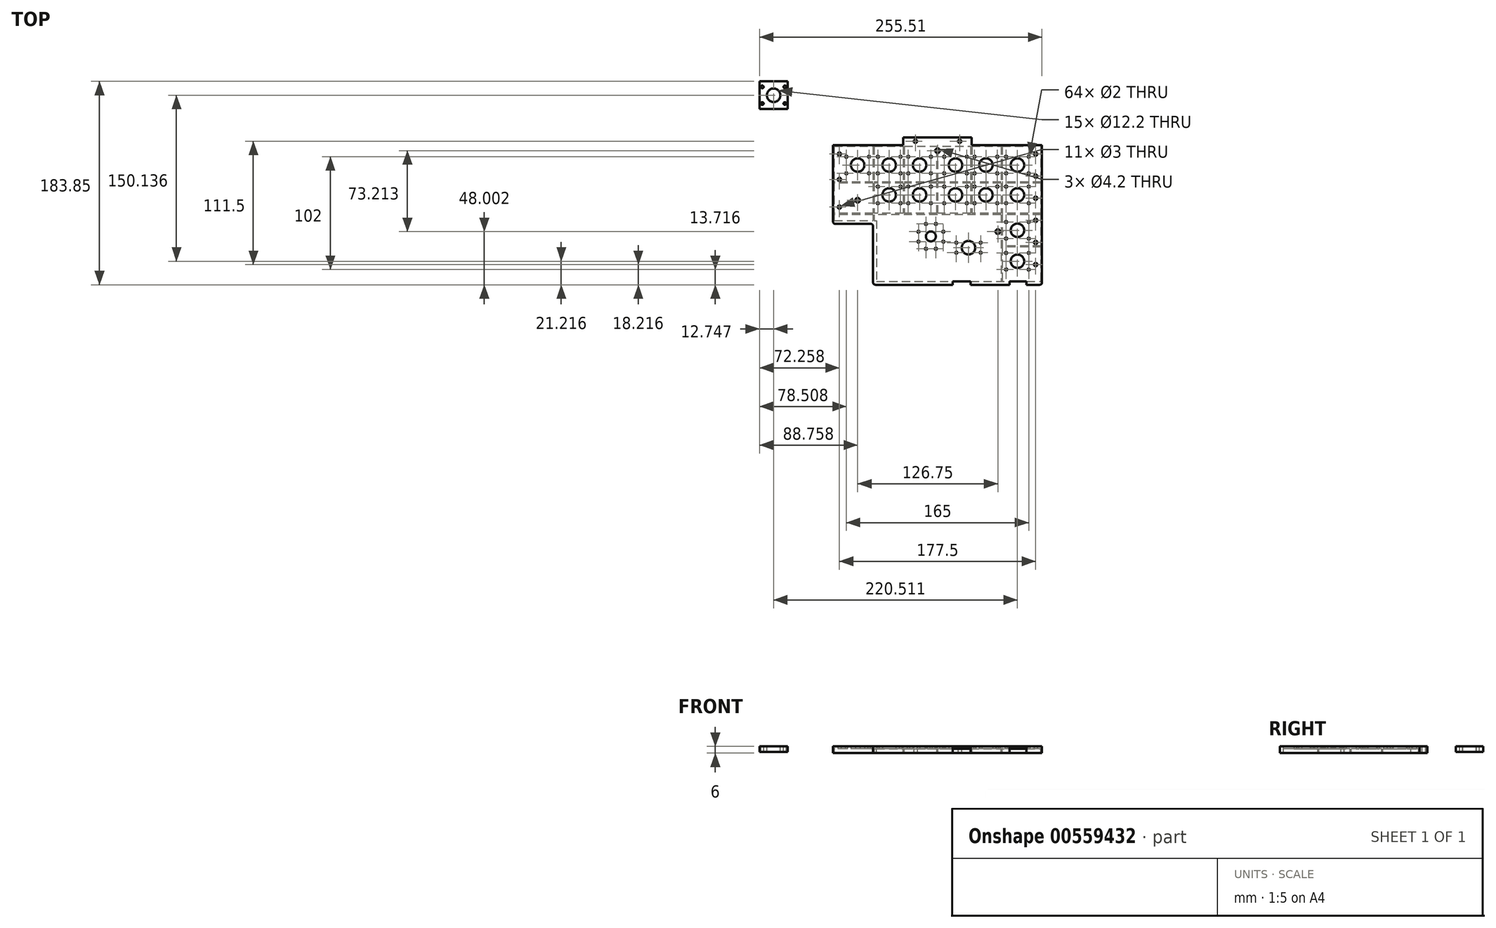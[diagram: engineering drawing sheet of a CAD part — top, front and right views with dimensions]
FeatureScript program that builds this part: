
annotation { "Feature Type Name" : "Feature", "Feature Type Description" : "" }
export const myFeature = defineFeature(function(context is Context, id is Id, definition is map)
    precondition{}
    {
        {
            var Q0;
            Q0=qCreatedBy(makeId("Top.planeOp"),FACE);
            var sketch = newSketch(context, id + "F0", { "sketchPlane" : qUnion([Q0])});
            skLineSegment(sketch, "E0.bottom", {"start": v(3.56, -143.75) * mm, "end": v(29.06, -143.75) * mm, "construction": true});
            skLineSegment(sketch, "E0.top", {"start": v(3.56, -173.75) * mm, "end": v(29.06, -173.75) * mm, "construction": true});
            skLineSegment(sketch, "E0.left", {"start": v(3.56, -143.75) * mm, "end": v(3.56, -173.75) * mm, "construction": true});
            skLineSegment(sketch, "E0.right", {"start": v(29.06, -143.75) * mm, "end": v(29.06, -173.75) * mm, "construction": true});
            skLineSegment(sketch, "E1.bottom", {"start": v(32.06, -143.75) * mm, "end": v(57.56, -143.75) * mm, "construction": true});
            skLineSegment(sketch, "E1.top", {"start": v(32.06, -173.75) * mm, "end": v(57.56, -173.75) * mm, "construction": true});
            skLineSegment(sketch, "E1.left", {"start": v(32.06, -143.75) * mm, "end": v(32.06, -173.75) * mm, "construction": true});
            skLineSegment(sketch, "E1.right", {"start": v(57.56, -143.75) * mm, "end": v(57.56, -173.75) * mm, "construction": true});
            skLineSegment(sketch, "E2.bottom", {"start": v(119.56, -143.75) * mm, "end": v(145.06, -143.75) * mm, "construction": true});
            skLineSegment(sketch, "E2.top", {"start": v(119.56, -173.75) * mm, "end": v(145.06, -173.75) * mm, "construction": true});
            skLineSegment(sketch, "E2.left", {"start": v(119.56, -143.75) * mm, "end": v(119.56, -173.75) * mm, "construction": true});
            skLineSegment(sketch, "E2.right", {"start": v(145.06, -143.75) * mm, "end": v(145.06, -173.75) * mm, "construction": true});
            skLineSegment(sketch, "E3.bottom", {"start": v(148.06, -143.75) * mm, "end": v(173.56, -143.75) * mm, "construction": true});
            skLineSegment(sketch, "E3.top", {"start": v(148.06, -173.75) * mm, "end": v(173.56, -173.75) * mm, "construction": true});
            skLineSegment(sketch, "E3.left", {"start": v(148.06, -143.75) * mm, "end": v(148.06, -173.75) * mm, "construction": true});
            skLineSegment(sketch, "E3.right", {"start": v(173.56, -143.75) * mm, "end": v(173.56, -173.75) * mm, "construction": true});
            skLineSegment(sketch, "E4.top", {"start": v(148.06, -206.75) * mm, "end": v(173.56, -206.75) * mm, "construction": true});
            skLineSegment(sketch, "E5.bottom", {"start": v(148.06, -209.25) * mm, "end": v(173.56, -209.25) * mm, "construction": true});
            skLineSegment(sketch, "E5.top", {"start": v(148.06, -239.25) * mm, "end": v(173.56, -239.25) * mm, "construction": true});
            skLineSegment(sketch, "E5.left", {"start": v(148.06, -209.25) * mm, "end": v(148.06, -239.25) * mm, "construction": true});
            skLineSegment(sketch, "E5.right", {"start": v(173.56, -209.25) * mm, "end": v(173.56, -239.25) * mm, "construction": true});
            skLineSegment(sketch, "E6.bottom", {"start": v(-4.94, -140.75) * mm, "end": v(182.06, -140.75) * mm});
            skLineSegment(sketch, "E6.top", {"start": v(33.28, -263.97) * mm, "end": v(182.06, -263.97) * mm});
            skLineSegment(sketch, "E6.left", {"start": v(-4.94, -140.75) * mm, "end": v(-4.94, -208.97) * mm});
            skLineSegment(sketch, "E6.right", {"start": v(182.06, -140.75) * mm, "end": v(182.06, -263.97) * mm});
            skLineSegment(sketch, "E7", {"start": v(-4.94, -208.97) * mm, "end": v(33.28, -208.97) * mm});
            skLineSegment(sketch, "E8", {"start": v(33.28, -208.97) * mm, "end": v(33.28, -263.97) * mm});
            skLineSegment(sketch, "E9.bottom", {"start": v(-67.45, -83.12) * mm, "end": v(-51.95, -83.12) * mm});
            skLineSegment(sketch, "E9.top", {"start": v(-67.45, -108.12) * mm, "end": v(-51.95, -108.12) * mm});
            skLineSegment(sketch, "E9.left", {"start": v(-67.45, -83.12) * mm, "end": v(-67.45, -108.12) * mm});
            skLineSegment(sketch, "E9.right", {"start": v(-51.95, -83.12) * mm, "end": v(-51.95, -108.12) * mm});
            skLineSegment(sketch, "E10.bottom", {"start": v(-51.95, -83.12) * mm, "end": v(-46.95, -83.12) * mm});
            skLineSegment(sketch, "E10.top", {"start": v(-51.95, -108.12) * mm, "end": v(-46.95, -108.12) * mm});
            skLineSegment(sketch, "E10.right", {"start": v(-46.95, -83.12) * mm, "end": v(-46.95, -108.12) * mm});
            skLineSegment(sketch, "E11.bottom", {"start": v(-67.45, -83.12) * mm, "end": v(-72.45, -83.12) * mm});
            skLineSegment(sketch, "E11.top", {"start": v(-67.45, -108.12) * mm, "end": v(-72.45, -108.12) * mm});
            skLineSegment(sketch, "E11.right", {"start": v(-72.45, -83.12) * mm, "end": v(-72.45, -108.12) * mm});
            skCircle(sketch, "E12", {"center": v(-59.7, -95.62) * mm, "radius": 6.1 * mm});
            skPoint(sketch, "E12.centerSnap0", {"position": v(-67.45, -95.62) * mm});
            skPoint(sketch, "E12.centerSnap1", {"position": v(-59.7, -83.12) * mm});
            skCircle(sketch, "E13", {"center": v(-69.95, -88.12) * mm, "radius": 1.25 * mm});
            skPoint(sketch, "E13.centerSnap0", {"position": v(-69.95, -83.12) * mm});
            skCircle(sketch, "E14", {"center": v(-69.95, -103.12) * mm, "radius": 1.25 * mm});
            skCircle(sketch, "E15", {"center": v(-49.45, -88.12) * mm, "radius": 1.25 * mm});
            skPoint(sketch, "E15.centerSnap0", {"position": v(-49.45, -83.12) * mm});
            skCircle(sketch, "E16", {"center": v(-49.45, -103.12) * mm, "radius": 1.25 * mm});
            skLineSegment(sketch, "E17.bottom", {"start": v(3.56, -146.25) * mm, "end": v(8.56, -146.25) * mm, "construction": true});
            skLineSegment(sketch, "E17.top", {"start": v(3.56, -171.25) * mm, "end": v(8.56, -171.25) * mm, "construction": true});
            skLineSegment(sketch, "E17.left", {"start": v(3.56, -146.25) * mm, "end": v(3.56, -171.25) * mm, "construction": true});
            skLineSegment(sketch, "E17.right", {"start": v(8.56, -146.25) * mm, "end": v(8.56, -171.25) * mm, "construction": true});
            skLineSegment(sketch, "E18.bottom", {"start": v(29.06, -146.25) * mm, "end": v(24.06, -146.25) * mm, "construction": true});
            skLineSegment(sketch, "E18.top", {"start": v(29.06, -171.25) * mm, "end": v(24.06, -171.25) * mm, "construction": true});
            skLineSegment(sketch, "E18.left", {"start": v(29.06, -146.25) * mm, "end": v(29.06, -171.25) * mm, "construction": true});
            skLineSegment(sketch, "E18.right", {"start": v(24.06, -146.25) * mm, "end": v(24.06, -171.25) * mm, "construction": true});
            skCircle(sketch, "E19", {"center": v(6.06, -151.25) * mm, "radius": 1 * mm});
            skPoint(sketch, "E19.centerSnap0", {"position": v(6.06, -146.25) * mm});
            skCircle(sketch, "E20", {"center": v(6.06, -166.25) * mm, "radius": 1 * mm});
            skCircle(sketch, "E21", {"center": v(16.3, -158.75) * mm, "radius": 6.1 * mm});
            skPoint(sketch, "E21.centerSnap0", {"position": v(8.56, -158.75) * mm});
            skPoint(sketch, "E21.centerSnap1", {"position": v(16.3, -143.75) * mm});
            skCircle(sketch, "E22", {"center": v(26.56, -151.25) * mm, "radius": 1 * mm});
            skPoint(sketch, "E22.centerSnap0", {"position": v(26.56, -146.25) * mm});
            skCircle(sketch, "E23", {"center": v(26.56, -166.25) * mm, "radius": 1 * mm});
            skCircle(sketch, "E24", {"center": v(105.56, -228.97) * mm, "radius": 1 * mm});
            skCircle(sketch, "E25", {"center": v(105.56, -237.97) * mm, "radius": 1 * mm});
            skCircle(sketch, "E26", {"center": v(127.56, -228.97) * mm, "radius": 1 * mm});
            skCircle(sketch, "E27", {"center": v(127.56, -237.97) * mm, "radius": 1 * mm});
            skLineSegment(sketch, "E28.bottom", {"start": v(151.56, -240.25) * mm, "end": v(173.56, -240.25) * mm, "construction": true});
            skLineSegment(sketch, "E28.top", {"start": v(151.56, -262.25) * mm, "end": v(173.56, -262.25) * mm, "construction": true});
            skLineSegment(sketch, "E28.left", {"start": v(151.56, -240.25) * mm, "end": v(151.56, -262.25) * mm, "construction": true});
            skLineSegment(sketch, "E28.right", {"start": v(173.56, -240.25) * mm, "end": v(173.56, -262.25) * mm, "construction": true});
            skLineSegment(sketch, "E29.bottom", {"start": v(154.8, -239.75) * mm, "end": v(166.8, -239.75) * mm, "construction": true});
            skLineSegment(sketch, "E29.top", {"start": v(154.8, -251.75) * mm, "end": v(166.8, -251.75) * mm, "construction": true});
            skLineSegment(sketch, "E29.left", {"start": v(154.8, -239.75) * mm, "end": v(154.8, -251.75) * mm, "construction": true});
            skLineSegment(sketch, "E29.right", {"start": v(166.8, -239.75) * mm, "end": v(166.8, -251.75) * mm, "construction": true});
            skLineSegment(sketch, "E30.bottom", {"start": v(32.06, -146.25) * mm, "end": v(37.06, -146.25) * mm, "construction": true});
            skLineSegment(sketch, "E30.top", {"start": v(32.06, -171.25) * mm, "end": v(37.06, -171.25) * mm, "construction": true});
            skLineSegment(sketch, "E30.left", {"start": v(32.06, -146.25) * mm, "end": v(32.06, -171.25) * mm, "construction": true});
            skLineSegment(sketch, "E30.right", {"start": v(37.06, -146.25) * mm, "end": v(37.06, -171.25) * mm, "construction": true});
            skLineSegment(sketch, "E31.bottom", {"start": v(57.56, -146.25) * mm, "end": v(52.56, -146.25) * mm, "construction": true});
            skLineSegment(sketch, "E31.top", {"start": v(57.56, -171.25) * mm, "end": v(52.56, -171.25) * mm, "construction": true});
            skLineSegment(sketch, "E31.left", {"start": v(57.56, -146.25) * mm, "end": v(57.56, -171.25) * mm, "construction": true});
            skLineSegment(sketch, "E31.right", {"start": v(52.56, -146.25) * mm, "end": v(52.56, -171.25) * mm, "construction": true});
            skCircle(sketch, "E32", {"center": v(34.56, -151.25) * mm, "radius": 1 * mm});
            skPoint(sketch, "E32.centerSnap0", {"position": v(34.56, -146.25) * mm});
            skCircle(sketch, "E33", {"center": v(34.56, -166.25) * mm, "radius": 1 * mm});
            skCircle(sketch, "E34", {"center": v(55.06, -151.25) * mm, "radius": 1 * mm});
            skPoint(sketch, "E34.centerSnap0", {"position": v(55.06, -146.25) * mm});
            skCircle(sketch, "E35", {"center": v(55.06, -166.25) * mm, "radius": 1 * mm});
            skCircle(sketch, "E36", {"center": v(44.8, -158.75) * mm, "radius": 6.1 * mm});
            skPoint(sketch, "E36.centerSnap0", {"position": v(37.06, -158.75) * mm});
            skPoint(sketch, "E36.centerSnap1", {"position": v(44.8, -143.75) * mm});
            skLineSegment(sketch, "E37.bottom", {"start": v(119.56, -146.25) * mm, "end": v(124.56, -146.25) * mm, "construction": true});
            skLineSegment(sketch, "E37.top", {"start": v(119.56, -171.25) * mm, "end": v(124.56, -171.25) * mm, "construction": true});
            skLineSegment(sketch, "E37.left", {"start": v(119.56, -146.25) * mm, "end": v(119.56, -171.25) * mm, "construction": true});
            skLineSegment(sketch, "E37.right", {"start": v(124.56, -146.25) * mm, "end": v(124.56, -171.25) * mm, "construction": true});
            skLineSegment(sketch, "E38.bottom", {"start": v(145.06, -146.25) * mm, "end": v(140.06, -146.25) * mm, "construction": true});
            skLineSegment(sketch, "E38.top", {"start": v(145.06, -171.25) * mm, "end": v(140.06, -171.25) * mm, "construction": true});
            skLineSegment(sketch, "E38.left", {"start": v(145.06, -146.25) * mm, "end": v(145.06, -171.25) * mm, "construction": true});
            skLineSegment(sketch, "E38.right", {"start": v(140.06, -146.25) * mm, "end": v(140.06, -171.25) * mm, "construction": true});
            skLineSegment(sketch, "E39.bottom", {"start": v(148.06, -146.25) * mm, "end": v(153.06, -146.25) * mm, "construction": true});
            skLineSegment(sketch, "E39.top", {"start": v(148.06, -171.25) * mm, "end": v(153.06, -171.25) * mm, "construction": true});
            skLineSegment(sketch, "E39.left", {"start": v(148.06, -146.25) * mm, "end": v(148.06, -171.25) * mm, "construction": true});
            skLineSegment(sketch, "E39.right", {"start": v(153.06, -146.25) * mm, "end": v(153.06, -171.25) * mm, "construction": true});
            skLineSegment(sketch, "E40.bottom", {"start": v(173.56, -146.25) * mm, "end": v(168.56, -146.25) * mm, "construction": true});
            skLineSegment(sketch, "E40.top", {"start": v(173.56, -171.25) * mm, "end": v(168.56, -171.25) * mm, "construction": true});
            skLineSegment(sketch, "E40.left", {"start": v(173.56, -146.25) * mm, "end": v(173.56, -171.25) * mm, "construction": true});
            skLineSegment(sketch, "E40.right", {"start": v(168.56, -146.25) * mm, "end": v(168.56, -171.25) * mm, "construction": true});
            skLineSegment(sketch, "E41.top", {"start": v(148.06, -204.25) * mm, "end": v(153.06, -204.25) * mm, "construction": true});
            skLineSegment(sketch, "E42.top", {"start": v(173.56, -204.25) * mm, "end": v(168.56, -204.25) * mm, "construction": true});
            skLineSegment(sketch, "E43.bottom", {"start": v(148.06, -205.25) * mm, "end": v(153.06, -205.25) * mm, "construction": true});
            skLineSegment(sketch, "E43.top", {"start": v(148.06, -230.25) * mm, "end": v(153.06, -230.25) * mm, "construction": true});
            skLineSegment(sketch, "E43.left", {"start": v(148.06, -205.25) * mm, "end": v(148.06, -230.25) * mm, "construction": true});
            skLineSegment(sketch, "E43.right", {"start": v(153.06, -205.25) * mm, "end": v(153.06, -230.25) * mm, "construction": true});
            skLineSegment(sketch, "E44.bottom", {"start": v(173.56, -205.25) * mm, "end": v(168.56, -205.25) * mm, "construction": true});
            skLineSegment(sketch, "E44.top", {"start": v(173.56, -230.25) * mm, "end": v(168.56, -230.25) * mm, "construction": true});
            skLineSegment(sketch, "E44.left", {"start": v(173.56, -205.25) * mm, "end": v(173.56, -230.25) * mm, "construction": true});
            skLineSegment(sketch, "E44.right", {"start": v(168.56, -205.25) * mm, "end": v(168.56, -230.25) * mm, "construction": true});
            skCircle(sketch, "E45", {"center": v(62.06, -178.25) * mm, "radius": 1 * mm});
            skCircle(sketch, "E46", {"center": v(62.06, -193.25) * mm, "radius": 1 * mm});
            skCircle(sketch, "E47", {"center": v(82.56, -178.25) * mm, "radius": 1 * mm});
            skCircle(sketch, "E48", {"center": v(82.56, -193.25) * mm, "radius": 1 * mm});
            skCircle(sketch, "E49", {"center": v(72.3, -185.75) * mm, "radius": 6.1 * mm});
            skCircle(sketch, "E50", {"center": v(82.56, -223.25) * mm, "radius": 4.5 * mm});
            skCircle(sketch, "E51", {"center": v(71.3, -219) * mm, "radius": 1 * mm});
            skCircle(sketch, "E52", {"center": v(71.3, -228) * mm, "radius": 1 * mm});
            skCircle(sketch, "E53", {"center": v(93.8, -219) * mm, "radius": 1 * mm});
            skCircle(sketch, "E54", {"center": v(93.8, -228) * mm, "radius": 1 * mm});
            skCircle(sketch, "E55", {"center": v(94.56, -178.25) * mm, "radius": 1 * mm});
            skCircle(sketch, "E56", {"center": v(94.56, -193.25) * mm, "radius": 1 * mm});
            skCircle(sketch, "E57", {"center": v(115.06, -178.25) * mm, "radius": 1 * mm});
            skCircle(sketch, "E58", {"center": v(115.06, -193.25) * mm, "radius": 1 * mm});
            skCircle(sketch, "E59", {"center": v(122.06, -151.25) * mm, "radius": 1 * mm});
            skPoint(sketch, "E59.centerSnap0", {"position": v(122.06, -146.25) * mm});
            skCircle(sketch, "E60", {"center": v(122.06, -166.25) * mm, "radius": 1 * mm});
            skCircle(sketch, "E61", {"center": v(132.3, -158.75) * mm, "radius": 6.1 * mm});
            skPoint(sketch, "E61.centerSnap0", {"position": v(124.56, -158.75) * mm});
            skPoint(sketch, "E61.centerSnap1", {"position": v(132.3, -143.75) * mm});
            skCircle(sketch, "E62", {"center": v(142.56, -151.25) * mm, "radius": 1 * mm});
            skPoint(sketch, "E62.centerSnap0", {"position": v(142.56, -146.25) * mm});
            skCircle(sketch, "E63", {"center": v(142.56, -166.25) * mm, "radius": 1 * mm});
            skCircle(sketch, "E64", {"center": v(150.56, -151.25) * mm, "radius": 1 * mm});
            skPoint(sketch, "E64.centerSnap0", {"position": v(150.56, -146.25) * mm});
            skCircle(sketch, "E65", {"center": v(150.56, -166.25) * mm, "radius": 1 * mm});
            skCircle(sketch, "E66", {"center": v(171.06, -151.25) * mm, "radius": 1 * mm});
            skPoint(sketch, "E66.centerSnap0", {"position": v(171.06, -146.25) * mm});
            skCircle(sketch, "E67", {"center": v(171.06, -166.25) * mm, "radius": 1 * mm});
            skCircle(sketch, "E68", {"center": v(160.8, -158.75) * mm, "radius": 6.1 * mm});
            skPoint(sketch, "E68.centerSnap0", {"position": v(153.06, -158.75) * mm});
            skPoint(sketch, "E68.centerSnap1", {"position": v(160.8, -143.75) * mm});
            skCircle(sketch, "E69", {"center": v(16.3, -190.57) * mm, "radius": 2.1 * mm});
            skCircle(sketch, "E70", {"center": v(143.06, -218.97) * mm, "radius": 2.1 * mm});
            skCircle(sketch, "E71", {"center": v(150.56, -210.25) * mm, "radius": 1 * mm});
            skPoint(sketch, "E71.centerSnap0", {"position": v(150.56, -205.25) * mm});
            skCircle(sketch, "E72", {"center": v(150.56, -225.25) * mm, "radius": 1 * mm});
            skCircle(sketch, "E73", {"center": v(171.06, -210.25) * mm, "radius": 1 * mm});
            skPoint(sketch, "E73.centerSnap0", {"position": v(171.06, -205.25) * mm});
            skCircle(sketch, "E74", {"center": v(171.06, -225.25) * mm, "radius": 1 * mm});
            skCircle(sketch, "E75", {"center": v(160.8, -217.75) * mm, "radius": 6.1 * mm});
            skPoint(sketch, "E75.centerSnap0", {"position": v(153.06, -217.75) * mm});
            skCircle(sketch, "E76", {"center": v(160.8, -245.75) * mm, "radius": 6.1 * mm});
            skPoint(sketch, "E76.centerSnap0", {"position": v(160.8, -239.75) * mm});
            skPoint(sketch, "E76.centerSnap1", {"position": v(154.8, -245.75) * mm});
            skCircle(sketch, "E77", {"center": v(-0.2, -148.75) * mm, "radius": 1.5 * mm});
            skCircle(sketch, "E78", {"center": v(-0.2, -171.75) * mm, "radius": 1.5 * mm});
            skCircle(sketch, "E79", {"center": v(177.3, -208.75) * mm, "radius": 1.5 * mm});
            skCircle(sketch, "E80", {"center": v(177.3, -228.75) * mm, "radius": 1.5 * mm});
            skCircle(sketch, "E81", {"center": v(177.3, -248.75) * mm, "radius": 1.5 * mm});
            skCircle(sketch, "E82", {"center": v(177.3, -168.75) * mm, "radius": 1.5 * mm});
            skCircle(sketch, "E83", {"center": v(177.3, -188.75) * mm, "radius": 1.5 * mm});
            skCircle(sketch, "E84", {"center": v(177.3, -148.75) * mm, "radius": 1.5 * mm});
            skCircle(sketch, "E85", {"center": v(150.56, -238.25) * mm, "radius": 1 * mm});
            skCircle(sketch, "E86", {"center": v(150.56, -253.25) * mm, "radius": 1 * mm});
            skCircle(sketch, "E87", {"center": v(171.06, -238.25) * mm, "radius": 1 * mm});
            skCircle(sketch, "E88", {"center": v(171.06, -253.25) * mm, "radius": 1 * mm});
            skCircle(sketch, "E89", {"center": v(-0.2, -196.75) * mm, "radius": 1.5 * mm});
            skLineSegment(sketch, "E90.bottom", {"start": v(58.56, -140.75) * mm, "end": v(118.56, -140.75) * mm});
            skLineSegment(sketch, "E90.top", {"start": v(58.56, -133.75) * mm, "end": v(118.56, -133.75) * mm});
            skLineSegment(sketch, "E90.left", {"start": v(58.56, -140.75) * mm, "end": v(58.56, -133.75) * mm});
            skLineSegment(sketch, "E90.right", {"start": v(118.56, -140.75) * mm, "end": v(118.56, -133.75) * mm});
            skCircle(sketch, "E91", {"center": v(68.56, -137.25) * mm, "radius": 1.5 * mm});
            skCircle(sketch, "E92", {"center": v(108.56, -137.25) * mm, "radius": 1.5 * mm});
            skCircle(sketch, "E93", {"center": v(116.56, -233.47) * mm, "radius": 6.1 * mm});
            skCircle(sketch, "E94", {"center": v(82.56, -223.25) * mm, "radius": 12.5 * mm, "construction": true});
            skCircle(sketch, "E95", {"center": v(44.8, -185.75) * mm, "radius": 6.1 * mm});
            skCircle(sketch, "E96", {"center": v(34.56, -178.25) * mm, "radius": 1 * mm});
            skCircle(sketch, "E97", {"center": v(34.56, -193.25) * mm, "radius": 1 * mm});
            skCircle(sketch, "E98", {"center": v(55.06, -178.25) * mm, "radius": 1 * mm});
            skCircle(sketch, "E99", {"center": v(55.06, -193.25) * mm, "radius": 1 * mm});
            skCircle(sketch, "E100", {"center": v(122.06, -193.25) * mm, "radius": 1 * mm});
            skCircle(sketch, "E101", {"center": v(142.56, -193.25) * mm, "radius": 1 * mm});
            skLineSegment(sketch, "E102", {"start": v(223.04, -262.25) * mm, "end": v(194.25, -262.25) * mm, "construction": true});
            skCircle(sketch, "E103", {"center": v(78.06, -212) * mm, "radius": 1 * mm});
            skCircle(sketch, "E104", {"center": v(87.06, -212) * mm, "radius": 1 * mm});
            skCircle(sketch, "E105", {"center": v(78.06, -234.5) * mm, "radius": 1 * mm});
            skCircle(sketch, "E106", {"center": v(87.06, -234.5) * mm, "radius": 1 * mm});
            skCircle(sketch, "E107", {"center": v(104.8, -185.75) * mm, "radius": 6.1 * mm});
            skCircle(sketch, "E108", {"center": v(132.3, -185.75) * mm, "radius": 6.1 * mm});
            skCircle(sketch, "E109", {"center": v(122.06, -178.25) * mm, "radius": 1 * mm});
            skCircle(sketch, "E110", {"center": v(142.56, -178.25) * mm, "radius": 1 * mm});
            skCircle(sketch, "E111", {"center": v(160.8, -185.75) * mm, "radius": 6.1 * mm});
            skCircle(sketch, "E112", {"center": v(150.56, -178.25) * mm, "radius": 1 * mm});
            skCircle(sketch, "E113", {"center": v(150.56, -193.25) * mm, "radius": 1 * mm});
            skCircle(sketch, "E114", {"center": v(171.06, -178.25) * mm, "radius": 1 * mm});
            skPoint(sketch, "E114.centerSnap0", {"position": v(171.06, -171.25) * mm});
            skCircle(sketch, "E115", {"center": v(171.06, -193.25) * mm, "radius": 1 * mm});
            skCircle(sketch, "E116", {"center": v(104.8, -158.75) * mm, "radius": 6.1 * mm});
            skCircle(sketch, "E117", {"center": v(115.06, -151.25) * mm, "radius": 1 * mm});
            skCircle(sketch, "E118", {"center": v(115.06, -166.25) * mm, "radius": 1 * mm});
            skCircle(sketch, "E119", {"center": v(94.56, -151.25) * mm, "radius": 1 * mm});
            skCircle(sketch, "E120", {"center": v(94.56, -166.25) * mm, "radius": 1 * mm});
            skCircle(sketch, "E121", {"center": v(72.3, -158.75) * mm, "radius": 6.1 * mm});
            skCircle(sketch, "E122", {"center": v(82.56, -151.25) * mm, "radius": 1 * mm});
            skCircle(sketch, "E123", {"center": v(82.56, -166.25) * mm, "radius": 1 * mm});
            skCircle(sketch, "E124", {"center": v(62.06, -151.25) * mm, "radius": 1 * mm});
            skCircle(sketch, "E125", {"center": v(62.06, -166.25) * mm, "radius": 1 * mm});
            skCircle(sketch, "E126", {"center": v(88.56, -145.75) * mm, "radius": 2.1 * mm});
            skSolve(sketch);
        }
        {
            var Q0;
            Q0=makeQuery(id+"F0.imprint","IMPRINT",FACE,{"disambiguationData":[TD([[makeQuery(id+"F0.imprint","IMPRINT",EDGE,{"derivedFrom":sQuery(id+"F0.wireOp",EDGE,"E9.bottom")}),-1.0]])]});
            var Q1;
            Q1=makeQuery(id+"F0.imprint","IMPRINT",FACE,{"disambiguationData":[TD([[makeQuery(id+"F0.imprint","IMPRINT",EDGE,{"derivedFrom":sQuery(id+"F0.wireOp",EDGE,"E11.bottom")}),1.0]])]});
            var Q2;
            Q2=makeQuery(id+"F0.imprint","IMPRINT",FACE,{"disambiguationData":[TD([[makeQuery(id+"F0.imprint","IMPRINT",EDGE,{"derivedFrom":sQuery(id+"F0.wireOp",EDGE,"E10.bottom")}),-1.0]])]});
            extrude(context, id + "F1", {"entities" : qUnion([Q0, Q1, Q2]), "oppositeDirection" : true, "depth" : 3 * mm});
        }
        {
            var Q0;
            Q0=qSketchRegion(id+"F0",true);
            extrude(context, id + "F2", {"entities" : qUnion([Q0]), "operationType" : NewBodyOperationType.ADD, "depth" : 2 * mm});
        }
        {
            var Q0;
            Q0=makeQuery(id+"F0.imprint","IMPRINT",FACE,{"disambiguationData":[TD([[makeQuery(id+"F0.imprint","IMPRINT",EDGE,{"derivedFrom":sQuery(id+"F0.wireOp",EDGE,"E6.bottom")}),-1.0]])]});
            var sketch = newSketch(context, id + "F3", { "sketchPlane" : qUnion([Q0])});
            skLineSegment(sketch, "E127", {"start": v(191, -174) * mm, "end": v(196.06, -174) * mm, "construction": true});
            skLineSegment(sketch, "E128", {"start": v(187.13, -202.5) * mm, "end": v(195.16, -202.5) * mm, "construction": true});
            skLineSegment(sketch, "E129", {"start": v(185.67, -231.87) * mm, "end": v(191.23, -231.87) * mm, "construction": true});
            skLineSegment(sketch, "E130", {"start": v(147.06, -137.55) * mm, "end": v(147.06, -134.13) * mm, "construction": true});
            skLineSegment(sketch, "E131", {"start": v(119.6, -132.5) * mm, "end": v(119.6, -129.45) * mm, "construction": true});
            skLineSegment(sketch, "E132", {"start": v(58.56, -132.83) * mm, "end": v(58.56, -129.85) * mm, "construction": true});
            skLineSegment(sketch, "E133", {"start": v(31.28, -136.19) * mm, "end": v(31.28, -132.5) * mm, "construction": true});
            skLineSegment(sketch, "E134.bottom", {"start": v(182.06, -174) * mm, "end": v(147.06, -174) * mm});
            skLineSegment(sketch, "E134.top", {"start": v(182.06, -175) * mm, "end": v(147.06, -175) * mm});
            skLineSegment(sketch, "E134.left", {"start": v(182.06, -174) * mm, "end": v(182.06, -175) * mm});
            skLineSegment(sketch, "E134.right", {"start": v(-4.94, -174) * mm, "end": v(-4.94, -175) * mm});
            skLineSegment(sketch, "E135.bottom", {"start": v(182.06, -202.5) * mm, "end": v(147.06, -202.5) * mm});
            skLineSegment(sketch, "E135.top", {"start": v(182.06, -203.5) * mm, "end": v(147.06, -203.5) * mm});
            skLineSegment(sketch, "E135.left", {"start": v(182.06, -202.5) * mm, "end": v(182.06, -203.5) * mm});
            skLineSegment(sketch, "E135.right", {"start": v(-4.94, -202.5) * mm, "end": v(-4.94, -203.5) * mm});
            skLineSegment(sketch, "E136", {"start": v(194.32, -140.75) * mm, "end": v(196.06, -263.96) * mm, "construction": true});
            skLineSegment(sketch, "E137", {"start": v(190.9, -263.96) * mm, "end": v(185.03, -263.96) * mm, "construction": true});
            skLineSegment(sketch, "E138.bottom", {"start": v(182.06, -231.87) * mm, "end": v(147.06, -231.87) * mm});
            skLineSegment(sketch, "E138.top", {"start": v(182.06, -232.87) * mm, "end": v(147.06, -232.87) * mm});
            skLineSegment(sketch, "E138.left", {"start": v(182.06, -231.87) * mm, "end": v(182.06, -232.87) * mm});
            skLineSegment(sketch, "E139", {"start": v(-4.94, -139.37) * mm, "end": v(-4.94, -137.02) * mm, "construction": true});
            skLineSegment(sketch, "E140", {"start": v(-7.3, -140.75) * mm, "end": v(-12.92, -140.75) * mm, "construction": true});
            skLineSegment(sketch, "E141.bottom", {"start": v(-4.94, -140.75) * mm, "end": v(146.06, -140.75) * mm});
            skLineSegment(sketch, "E141.top", {"start": v(-4.94, -141.75) * mm, "end": v(146.06, -141.75) * mm});
            skLineSegment(sketch, "E141.left", {"start": v(-4.94, -140.75) * mm, "end": v(-4.94, -141.75) * mm});
            skLineSegment(sketch, "E141.right", {"start": v(182.06, -140.75) * mm, "end": v(182.06, -141.75) * mm});
            skLineSegment(sketch, "E142.bottom", {"start": v(147.06, -140.75) * mm, "end": v(146.06, -140.75) * mm});
            skLineSegment(sketch, "E142.top", {"start": v(147.06, -263.96) * mm, "end": v(146.06, -263.96) * mm});
            skLineSegment(sketch, "E142.left", {"start": v(147.06, -141.75) * mm, "end": v(147.06, -174) * mm});
            skLineSegment(sketch, "E142.right", {"start": v(146.06, -141.75) * mm, "end": v(146.06, -174) * mm});
            skLineSegment(sketch, "E143.trimOffspring", {"start": v(147.06, -175) * mm, "end": v(147.06, -202.5) * mm});
            skLineSegment(sketch, "E144.trimOffspring", {"start": v(146.06, -174) * mm, "end": v(119.6, -174) * mm});
            skLineSegment(sketch, "E145.trimOffspring", {"start": v(146.06, -175) * mm, "end": v(146.06, -202.5) * mm});
            skLineSegment(sketch, "E146.trimOffspring", {"start": v(146.06, -175) * mm, "end": v(119.6, -175) * mm});
            skLineSegment(sketch, "E147.trimOffspring", {"start": v(146.06, -202.5) * mm, "end": v(119.6, -202.5) * mm});
            skLineSegment(sketch, "E148.trimOffspring", {"start": v(147.06, -203.5) * mm, "end": v(147.06, -231.87) * mm});
            skLineSegment(sketch, "E149.trimOffspring", {"start": v(146.06, -203.5) * mm, "end": v(58.56, -203.5) * mm});
            skLineSegment(sketch, "E150.trimOffspring", {"start": v(146.06, -203.5) * mm, "end": v(146.06, -263.96) * mm});
            skLineSegment(sketch, "E151.trimOffspring", {"start": v(147.06, -232.87) * mm, "end": v(147.06, -263.96) * mm});
            skLineSegment(sketch, "E152.trimOffspring", {"start": v(147.06, -140.75) * mm, "end": v(182.06, -140.75) * mm});
            skLineSegment(sketch, "E153.trimOffspring", {"start": v(147.06, -141.75) * mm, "end": v(182.06, -141.75) * mm});
            skLineSegment(sketch, "E154.bottom", {"start": v(119.6, -140.75) * mm, "end": v(118.6, -140.75) * mm});
            skLineSegment(sketch, "E154.left", {"start": v(119.6, -140.75) * mm, "end": v(119.6, -174) * mm});
            skLineSegment(sketch, "E154.right", {"start": v(118.6, -140.75) * mm, "end": v(118.6, -174) * mm});
            skLineSegment(sketch, "E155.top", {"start": v(89.06, -148.72) * mm, "end": v(88.06, -148.72) * mm});
            skLineSegment(sketch, "E155.left", {"start": v(89.06, -202.5) * mm, "end": v(89.06, -175) * mm});
            skLineSegment(sketch, "E155.right", {"start": v(88.06, -202.5) * mm, "end": v(88.06, -175) * mm});
            skLineSegment(sketch, "E156.bottom", {"start": v(58.56, -140.75) * mm, "end": v(57.56, -140.75) * mm});
            skLineSegment(sketch, "E156.left", {"start": v(58.56, -140.75) * mm, "end": v(58.56, -174) * mm});
            skLineSegment(sketch, "E156.right", {"start": v(57.56, -140.75) * mm, "end": v(57.56, -174) * mm});
            skLineSegment(sketch, "E157.trimOffspring", {"start": v(119.6, -175) * mm, "end": v(119.6, -202.5) * mm});
            skLineSegment(sketch, "E158.trimOffspring", {"start": v(118.6, -174) * mm, "end": v(89.06, -174) * mm});
            skLineSegment(sketch, "E159.trimOffspring", {"start": v(118.6, -175) * mm, "end": v(118.6, -202.5) * mm});
            skLineSegment(sketch, "E160.trimOffspring", {"start": v(118.6, -175) * mm, "end": v(89.06, -175) * mm});
            skLineSegment(sketch, "E161.trimOffspring", {"start": v(89.06, -174) * mm, "end": v(89.06, -148.72) * mm});
            skLineSegment(sketch, "E162.trimOffspring", {"start": v(88.06, -174) * mm, "end": v(58.56, -174) * mm});
            skLineSegment(sketch, "E163.trimOffspring", {"start": v(88.06, -174) * mm, "end": v(88.06, -148.72) * mm});
            skLineSegment(sketch, "E164.trimOffspring", {"start": v(88.06, -175) * mm, "end": v(58.56, -175) * mm});
            skLineSegment(sketch, "E165.trimOffspring", {"start": v(88.06, -202.5) * mm, "end": v(58.56, -202.5) * mm});
            skLineSegment(sketch, "E166.trimOffspring", {"start": v(118.6, -202.5) * mm, "end": v(89.06, -202.5) * mm});
            skLineSegment(sketch, "E167.bottom", {"start": v(31.28, -140.75) * mm, "end": v(30.28, -140.75) * mm});
            skLineSegment(sketch, "E167.left", {"start": v(31.28, -140.75) * mm, "end": v(31.28, -174) * mm});
            skLineSegment(sketch, "E167.right", {"start": v(30.28, -140.75) * mm, "end": v(30.28, -174) * mm});
            skLineSegment(sketch, "E168.trimOffspring", {"start": v(57.56, -202.5) * mm, "end": v(31.28, -202.5) * mm});
            skLineSegment(sketch, "E169.trimOffspring", {"start": v(58.56, -203.5) * mm, "end": v(31.28, -203.5) * mm});
            skLineSegment(sketch, "E170.trimOffspring", {"start": v(58.56, -175) * mm, "end": v(58.56, -202.5) * mm});
            skLineSegment(sketch, "E171.trimOffspring", {"start": v(57.56, -174) * mm, "end": v(31.28, -174) * mm});
            skLineSegment(sketch, "E172.trimOffspring", {"start": v(57.56, -175) * mm, "end": v(57.56, -202.5) * mm});
            skLineSegment(sketch, "E173.trimOffspring", {"start": v(57.56, -175) * mm, "end": v(31.28, -175) * mm});
            skLineSegment(sketch, "E174.trimOffspring", {"start": v(31.28, -175) * mm, "end": v(31.28, -202.5) * mm});
            skLineSegment(sketch, "E175.trimOffspring", {"start": v(30.28, -174) * mm, "end": v(-4.94, -174) * mm});
            skLineSegment(sketch, "E176.trimOffspring", {"start": v(30.28, -175) * mm, "end": v(30.28, -202.5) * mm});
            skLineSegment(sketch, "E177.trimOffspring", {"start": v(30.28, -175) * mm, "end": v(-4.94, -175) * mm});
            skLineSegment(sketch, "E178.trimOffspring", {"start": v(30.28, -202.5) * mm, "end": v(-4.94, -202.5) * mm});
            skLineSegment(sketch, "E179.top", {"start": v(31.28, -208.97) * mm, "end": v(30.28, -208.97) * mm});
            skLineSegment(sketch, "E179.left", {"start": v(31.28, -203.5) * mm, "end": v(31.28, -208.97) * mm});
            skLineSegment(sketch, "E179.right", {"start": v(30.28, -203.5) * mm, "end": v(30.28, -208.97) * mm});
            skLineSegment(sketch, "E180.trimOffspring", {"start": v(30.28, -203.5) * mm, "end": v(-4.94, -203.5) * mm});
            skLineSegment(sketch, "E181.bottom", {"start": v(99.56, -203.5) * mm, "end": v(98.56, -203.5) * mm});
            skSolve(sketch);
        }
        {
            var Q0;
            Q0=makeQuery(id+"F2.opExtrude","CAP_FACE",FACE,{"disambiguationData":[OSD([sQuery(id+"F0.wireOp",EDGE,"E6.bottom"),sQuery(id+"F0.wireOp",EDGE,"E6.top"),sQuery(id+"F0.wireOp",EDGE,"E6.left"),sQuery(id+"F0.wireOp",EDGE,"E6.right"),sQuery(id+"F0.wireOp",EDGE,"E7"),sQuery(id+"F0.wireOp",EDGE,"E8"),sQuery(id+"F0.wireOp",EDGE,"E19"),sQuery(id+"F0.wireOp",EDGE,"E20"),sQuery(id+"F0.wireOp",EDGE,"E21"),sQuery(id+"F0.wireOp",EDGE,"E22"),sQuery(id+"F0.wireOp",EDGE,"E23"),sQuery(id+"F0.wireOp",EDGE,"E24"),sQuery(id+"F0.wireOp",EDGE,"E25"),sQuery(id+"F0.wireOp",EDGE,"E26"),sQuery(id+"F0.wireOp",EDGE,"E27"),sQuery(id+"F0.wireOp",EDGE,"E32"),sQuery(id+"F0.wireOp",EDGE,"E33"),sQuery(id+"F0.wireOp",EDGE,"E34"),sQuery(id+"F0.wireOp",EDGE,"E35"),sQuery(id+"F0.wireOp",EDGE,"E36"),sQuery(id+"F0.wireOp",EDGE,"CMYmPeaI-4HkP-dSsT-ciCo-EBNArNxvabU4"),sQuery(id+"F0.wireOp",EDGE,"UfYHLVnG-ZsXc-hSsb-096B-xReGw4xjWMuN"),sQuery(id+"F0.wireOp",EDGE,"LR1Smqzz-4zCy-jBud-aIPe-T4FdCvFcucQ2"),sQuery(id+"F0.wireOp",EDGE,"ZbBtRst9-qfY5-xJJi-duYC-lclwT5zfDQth"),sQuery(id+"F0.wireOp",EDGE,"8mlmSCBx-nmsO-8ibw-fLZu-H13SXNY5Fta6"),sQuery(id+"F0.wireOp",EDGE,"E45"),sQuery(id+"F0.wireOp",EDGE,"E46"),sQuery(id+"F0.wireOp",EDGE,"E47"),sQuery(id+"F0.wireOp",EDGE,"E48"),sQuery(id+"F0.wireOp",EDGE,"E49"),sQuery(id+"F0.wireOp",EDGE,"E50"),sQuery(id+"F0.wireOp",EDGE,"E51"),sQuery(id+"F0.wireOp",EDGE,"E52"),sQuery(id+"F0.wireOp",EDGE,"E53"),sQuery(id+"F0.wireOp",EDGE,"E54"),sQuery(id+"F0.wireOp",EDGE,"VxGM9Us5-GGZY-iukY-QufE-Hgw7Eb7M8YLq"),sQuery(id+"F0.wireOp",EDGE,"SQwhu13T-8Qlf-M2A9-FjbU-sqE2fhrdCHsq"),sQuery(id+"F0.wireOp",EDGE,"boMX5wRL-iCUG-njbD-9Rz0-iznqWW2C3mA9"),sQuery(id+"F0.wireOp",EDGE,"8wUrnrco-ptQb-soB3-ZJPL-oLVazxcvUS0h"),sQuery(id+"F0.wireOp",EDGE,"HpmNjthl-ehj3-1CQD-7Ubw-BaRG0imoQFcp"),sQuery(id+"F0.wireOp",EDGE,"E55"),sQuery(id+"F0.wireOp",EDGE,"E56"),sQuery(id+"F0.wireOp",EDGE,"E57"),sQuery(id+"F0.wireOp",EDGE,"E58"),sQuery(id+"F0.wireOp",EDGE,"VaTJDDM9-VUwq-8Ub5-B3vK-8OZuGjwCmtKx"),sQuery(id+"F0.wireOp",EDGE,"E59"),sQuery(id+"F0.wireOp",EDGE,"E60"),sQuery(id+"F0.wireOp",EDGE,"E61"),sQuery(id+"F0.wireOp",EDGE,"E62"),sQuery(id+"F0.wireOp",EDGE,"E63"),sQuery(id+"F0.wireOp",EDGE,"E64"),sQuery(id+"F0.wireOp",EDGE,"E65"),sQuery(id+"F0.wireOp",EDGE,"E66"),sQuery(id+"F0.wireOp",EDGE,"E67"),sQuery(id+"F0.wireOp",EDGE,"E68"),sQuery(id+"F0.wireOp",EDGE,"FLjO8hJO-b9aV-ejTu-NQdn-92oojDJo2zOz"),sQuery(id+"F0.wireOp",EDGE,"a0hJ5jbA-nbqK-hj7D-t7WL-IcpDiukpPwzh"),sQuery(id+"F0.wireOp",EDGE,"Ryervvjx-vNoG-fDVS-CNAW-2For5iN3UFYN"),sQuery(id+"F0.wireOp",EDGE,"h7MID1Gx-mTQT-Sx65-6Eka-E6sNebulpS2X"),sQuery(id+"F0.wireOp",EDGE,"WRXfD2HC-k7r3-eJkd-8mHz-8ZkhsYc1BRgL"),sQuery(id+"F0.wireOp",EDGE,"E69"),sQuery(id+"F0.wireOp",EDGE,"E70"),sQuery(id+"F0.wireOp",EDGE,"E71"),sQuery(id+"F0.wireOp",EDGE,"E72"),sQuery(id+"F0.wireOp",EDGE,"E73"),sQuery(id+"F0.wireOp",EDGE,"E74"),sQuery(id+"F0.wireOp",EDGE,"E75"),sQuery(id+"F0.wireOp",EDGE,"i2m1gv8j-diLw-4k4K-fPdu-nWKSfx8HA4P4"),sQuery(id+"F0.wireOp",EDGE,"q3kUeOFW-MYc1-yF3y-feIh-HT3K9hYQvfPw"),sQuery(id+"F0.wireOp",EDGE,"E76"),sQuery(id+"F0.wireOp",EDGE,"0s6mQaFc-8NzZ-X89h-nX0r-AyVE9FRU5R3i"),sQuery(id+"F0.wireOp",EDGE,"E77"),sQuery(id+"F0.wireOp",EDGE,"OnnnS06f-s26S-AFDA-oTM6-wnMq7venfp2T"),sQuery(id+"F0.wireOp",EDGE,"V2efC4Jm-4NAF-VBiO-pQnY-etMWDclGv5un"),sQuery(id+"F0.wireOp",EDGE,"E78"),sQuery(id+"F0.wireOp",EDGE,"7M3HGg5D-aMQl-LYs1-MsCg-zVmLHFwYCo0C"),sQuery(id+"F0.wireOp",EDGE,"e6U4q213-1LtL-vwCs-wLTg-mGHH5etSdpE2"),sQuery(id+"F0.wireOp",EDGE,"E79"),sQuery(id+"F0.wireOp",EDGE,"E80"),sQuery(id+"F0.wireOp",EDGE,"E81"),sQuery(id+"F0.wireOp",EDGE,"E82"),sQuery(id+"F0.wireOp",EDGE,"R6Wk8btU-zCGi-4TmP-5Jjd-FV93XaIFImrj"),sQuery(id+"F0.wireOp",EDGE,"E83"),sQuery(id+"F0.wireOp",EDGE,"E84"),sQuery(id+"F0.wireOp",EDGE,"gRVzFYeP-EyGY-z86r-QQTZ-wZyysSSB34M7"),sQuery(id+"F0.wireOp",EDGE,"ylX56w3w-VO5M-fSch-uKYX-FYdjN5tmCMk0"),sQuery(id+"F0.wireOp",EDGE,"agFm78Yh-b6q2-hou8-vdYd-aVKsI7ZKnxmv"),sQuery(id+"F0.wireOp",EDGE,"Ipsl4LbN-QmTd-Wo4k-Iefa-eoOeaxQxMcxx"),sQuery(id+"F0.wireOp",EDGE,"aOvKBL3Z-v0oe-Nazm-0AOk-5JJxyVFELpqL"),sQuery(id+"F0.wireOp",EDGE,"PIPjAFRf-HRrE-UI3a-6rHr-U4BEnBnb3Jr0"),sQuery(id+"F0.wireOp",EDGE,"clCWdQkL-82pP-eXah-HGsn-A5WvFmz6JLAg"),sQuery(id+"F0.wireOp",EDGE,"E85"),sQuery(id+"F0.wireOp",EDGE,"E86"),sQuery(id+"F0.wireOp",EDGE,"E87"),sQuery(id+"F0.wireOp",EDGE,"E88"),sQuery(id+"F0.wireOp",EDGE,"2CZ2vCPZ-g25f-Aix0-Xy3j-dVw2FXJ3BshQ.bottom"),sQuery(id+"F0.wireOp",EDGE,"2CZ2vCPZ-g25f-Aix0-Xy3j-dVw2FXJ3BshQ.left"),sQuery(id+"F0.wireOp",EDGE,"2CZ2vCPZ-g25f-Aix0-Xy3j-dVw2FXJ3BshQ.right"),sQuery(id+"F0.wireOp",EDGE,"3PAsEz4y-MCME-JD8k-KRcV-DaMAZ5aYk3wh"),sQuery(id+"F0.wireOp",EDGE,"PkSCfb9l-bHuo-pSPV-febg-RSfLSyBgUNz0")])],"isStart":false});
            var sketch = newSketch(context, id + "F4", { "sketchPlane" : qUnion([Q0])});
            skLineSegment(sketch, "E182.bottom", {"start": v(-4.94, -140.75) * mm, "end": v(-5.94, -140.75) * mm});
            skLineSegment(sketch, "E182.top", {"start": v(-4.94, -208.97) * mm, "end": v(-5.94, -208.97) * mm});
            skLineSegment(sketch, "E182.left", {"start": v(-4.94, -140.75) * mm, "end": v(-4.94, -208.97) * mm});
            skLineSegment(sketch, "E182.right", {"start": v(-5.94, -140.75) * mm, "end": v(-5.94, -208.97) * mm});
            skLineSegment(sketch, "E183.bottom", {"start": v(-5.94, -208.97) * mm, "end": v(33.28, -208.97) * mm});
            skLineSegment(sketch, "E183.top", {"start": v(-5.94, -211.97) * mm, "end": v(33.28, -211.97) * mm});
            skLineSegment(sketch, "E183.left", {"start": v(-5.94, -208.97) * mm, "end": v(-5.94, -211.97) * mm});
            skLineSegment(sketch, "E183.right", {"start": v(33.28, -208.97) * mm, "end": v(33.28, -211.97) * mm});
            skLineSegment(sketch, "E184.bottom", {"start": v(33.28, -263.97) * mm, "end": v(30.28, -263.97) * mm});
            skLineSegment(sketch, "E184.top", {"start": v(33.28, -211.97) * mm, "end": v(30.28, -211.97) * mm});
            skLineSegment(sketch, "E184.left", {"start": v(33.28, -263.97) * mm, "end": v(33.28, -211.97) * mm});
            skLineSegment(sketch, "E184.right", {"start": v(30.28, -263.97) * mm, "end": v(30.28, -211.97) * mm});
            skLineSegment(sketch, "E185.bottom", {"start": v(182.06, -140.75) * mm, "end": v(183.06, -140.75) * mm});
            skLineSegment(sketch, "E185.top", {"start": v(182.06, -263.97) * mm, "end": v(183.06, -263.97) * mm});
            skLineSegment(sketch, "E185.left", {"start": v(182.06, -140.75) * mm, "end": v(182.06, -263.97) * mm});
            skLineSegment(sketch, "E185.right", {"start": v(183.06, -140.75) * mm, "end": v(183.06, -263.97) * mm});
            skLineSegment(sketch, "E186.bottom", {"start": v(183.06, -263.97) * mm, "end": v(169.06, -263.97) * mm});
            skLineSegment(sketch, "E186.top", {"start": v(183.06, -266.97) * mm, "end": v(169.06, -266.97) * mm});
            skLineSegment(sketch, "E186.left", {"start": v(183.06, -263.97) * mm, "end": v(183.06, -266.97) * mm});
            skLineSegment(sketch, "E186.right", {"start": v(169.06, -263.97) * mm, "end": v(169.06, -266.97) * mm});
            skLineSegment(sketch, "E187.bottom", {"start": v(153.56, -263.97) * mm, "end": v(118.56, -263.97) * mm});
            skLineSegment(sketch, "E187.top", {"start": v(153.56, -266.97) * mm, "end": v(118.56, -266.97) * mm});
            skLineSegment(sketch, "E187.left", {"start": v(153.56, -263.97) * mm, "end": v(153.56, -266.97) * mm});
            skLineSegment(sketch, "E187.right", {"start": v(118.56, -263.97) * mm, "end": v(118.56, -266.97) * mm});
            skLineSegment(sketch, "E188.bottom", {"start": v(30.28, -263.97) * mm, "end": v(102.28, -263.97) * mm});
            skLineSegment(sketch, "E188.top", {"start": v(30.28, -266.97) * mm, "end": v(102.28, -266.97) * mm});
            skLineSegment(sketch, "E188.left", {"start": v(30.28, -263.97) * mm, "end": v(30.28, -266.97) * mm});
            skLineSegment(sketch, "E188.right", {"start": v(102.28, -263.97) * mm, "end": v(102.28, -266.97) * mm});
            skLineSegment(sketch, "E189.bottom", {"start": v(118.56, -133.75) * mm, "end": v(119.56, -133.75) * mm});
            skLineSegment(sketch, "E189.top", {"start": v(118.56, -140.75) * mm, "end": v(119.56, -140.75) * mm});
            skLineSegment(sketch, "E189.left", {"start": v(118.56, -133.75) * mm, "end": v(118.56, -140.75) * mm});
            skLineSegment(sketch, "E189.right", {"start": v(119.56, -133.75) * mm, "end": v(119.56, -140.75) * mm});
            skLineSegment(sketch, "E190.bottom", {"start": v(58.56, -133.75) * mm, "end": v(57.56, -133.75) * mm});
            skLineSegment(sketch, "E190.top", {"start": v(58.56, -140.75) * mm, "end": v(57.56, -140.75) * mm});
            skLineSegment(sketch, "E190.left", {"start": v(58.56, -133.75) * mm, "end": v(58.56, -140.75) * mm});
            skLineSegment(sketch, "E190.right", {"start": v(57.56, -133.75) * mm, "end": v(57.56, -140.75) * mm});
            skSolve(sketch);
        }
        {
            var Q0;
            Q0=qSketchRegion(id+"F4",true);
            extrude(context, id + "F5", {"entities" : qUnion([Q0]), "operationType" : NewBodyOperationType.ADD, "oppositeDirection" : true, "depth" : 6 * mm});
        }
        {
            var Q0;
            Q0=makeQuery(id+"F5.opExtrude","SWEPT_EDGE",EDGE,{"disambiguationData":[OSD([sQuery(id+"F4.wireOp",EDGE,"E183.top"),sQuery(id+"F4.wireOp",EDGE,"E183.left")])]});
            var Q1;
            Q1=makeQuery(id+"F5.opExtrude","SWEPT_EDGE",EDGE,{"disambiguationData":[OSD([sQuery(id+"F4.wireOp",EDGE,"E183.top"),sQuery(id+"F4.wireOp",EDGE,"E184.top"),sQuery(id+"F4.wireOp",EDGE,"E184.right")])]});
            var Q2;
            Q2=makeQuery(id+"F5.opExtrude","SWEPT_EDGE",EDGE,{"disambiguationData":[OSD([sQuery(id+"F4.wireOp",EDGE,"E188.top"),sQuery(id+"F4.wireOp",EDGE,"E188.left")])]});
            var Q3;
            Q3=makeQuery(id+"F5.opExtrude","SWEPT_EDGE",EDGE,{"disambiguationData":[OSD([sQuery(id+"F4.wireOp",EDGE,"E186.top"),sQuery(id+"F4.wireOp",EDGE,"E186.left")])]});
            fillet(context, id + "F6", {"entities" : qUnion([Q0, Q1, Q2, Q3]), "radius" : 2 * mm, "tangentPropagation" : true, "allowEdgeOverflow" : false});
        }
        {
            var Q0;
            Q0=qSketchRegion(id+"F3",true);
            extrude(context, id + "F7", {"entities" : qUnion([Q0]), "operationType" : NewBodyOperationType.ADD, "oppositeDirection" : true, "depth" : 4 * mm});
        }
        {
            var Q0;
            {var subQ0=sQuery(id+"F0.wireOp",EDGE,"E92");var subQ1=sQuery(id+"F0.wireOp",EDGE,"E91");var subQ2=sQuery(id+"F0.wireOp",EDGE,"E90.top");Q0=makeQuery(id+"F7.boolean.opBoolean","SPLIT",FACE,{"disambiguationData":[TD([makeQuery(id+"F2.opExtrude","SWEPT_FACE",FACE,{"disambiguationData":[OSD([subQ2])]})])],"derivedFrom":makeQuery(id+"F2.opExtrude","CAP_FACE",FACE,{"disambiguationData":[OSD([sQuery(id+"F0.wireOp",EDGE,"E6.bottom"),sQuery(id+"F0.wireOp",EDGE,"E6.top"),sQuery(id+"F0.wireOp",EDGE,"E6.left"),sQuery(id+"F0.wireOp",EDGE,"E6.right"),sQuery(id+"F0.wireOp",EDGE,"E7"),sQuery(id+"F0.wireOp",EDGE,"E8"),sQuery(id+"F0.wireOp",EDGE,"E19"),sQuery(id+"F0.wireOp",EDGE,"E20"),sQuery(id+"F0.wireOp",EDGE,"E21"),sQuery(id+"F0.wireOp",EDGE,"E22"),sQuery(id+"F0.wireOp",EDGE,"E23"),sQuery(id+"F0.wireOp",EDGE,"E24"),sQuery(id+"F0.wireOp",EDGE,"E25"),sQuery(id+"F0.wireOp",EDGE,"E26"),sQuery(id+"F0.wireOp",EDGE,"E27"),sQuery(id+"F0.wireOp",EDGE,"E32"),sQuery(id+"F0.wireOp",EDGE,"E33"),sQuery(id+"F0.wireOp",EDGE,"E34"),sQuery(id+"F0.wireOp",EDGE,"E35"),sQuery(id+"F0.wireOp",EDGE,"E36"),sQuery(id+"F0.wireOp",EDGE,"CMYmPeaI-4HkP-dSsT-ciCo-EBNArNxvabU4"),sQuery(id+"F0.wireOp",EDGE,"UfYHLVnG-ZsXc-hSsb-096B-xReGw4xjWMuN"),sQuery(id+"F0.wireOp",EDGE,"LR1Smqzz-4zCy-jBud-aIPe-T4FdCvFcucQ2"),sQuery(id+"F0.wireOp",EDGE,"ZbBtRst9-qfY5-xJJi-duYC-lclwT5zfDQth"),sQuery(id+"F0.wireOp",EDGE,"8mlmSCBx-nmsO-8ibw-fLZu-H13SXNY5Fta6"),sQuery(id+"F0.wireOp",EDGE,"E45"),sQuery(id+"F0.wireOp",EDGE,"E46"),sQuery(id+"F0.wireOp",EDGE,"E47"),sQuery(id+"F0.wireOp",EDGE,"E48"),sQuery(id+"F0.wireOp",EDGE,"E49"),sQuery(id+"F0.wireOp",EDGE,"E50"),sQuery(id+"F0.wireOp",EDGE,"E51"),sQuery(id+"F0.wireOp",EDGE,"E52"),sQuery(id+"F0.wireOp",EDGE,"E53"),sQuery(id+"F0.wireOp",EDGE,"E54"),sQuery(id+"F0.wireOp",EDGE,"VxGM9Us5-GGZY-iukY-QufE-Hgw7Eb7M8YLq"),sQuery(id+"F0.wireOp",EDGE,"SQwhu13T-8Qlf-M2A9-FjbU-sqE2fhrdCHsq"),sQuery(id+"F0.wireOp",EDGE,"boMX5wRL-iCUG-njbD-9Rz0-iznqWW2C3mA9"),sQuery(id+"F0.wireOp",EDGE,"8wUrnrco-ptQb-soB3-ZJPL-oLVazxcvUS0h"),sQuery(id+"F0.wireOp",EDGE,"HpmNjthl-ehj3-1CQD-7Ubw-BaRG0imoQFcp"),sQuery(id+"F0.wireOp",EDGE,"E55"),sQuery(id+"F0.wireOp",EDGE,"E56"),sQuery(id+"F0.wireOp",EDGE,"E57"),sQuery(id+"F0.wireOp",EDGE,"E58"),sQuery(id+"F0.wireOp",EDGE,"E59"),sQuery(id+"F0.wireOp",EDGE,"E60"),sQuery(id+"F0.wireOp",EDGE,"E61"),sQuery(id+"F0.wireOp",EDGE,"E62"),sQuery(id+"F0.wireOp",EDGE,"E63"),sQuery(id+"F0.wireOp",EDGE,"E64"),sQuery(id+"F0.wireOp",EDGE,"E65"),sQuery(id+"F0.wireOp",EDGE,"E66"),sQuery(id+"F0.wireOp",EDGE,"E67"),sQuery(id+"F0.wireOp",EDGE,"E68"),sQuery(id+"F0.wireOp",EDGE,"E69"),sQuery(id+"F0.wireOp",EDGE,"E70"),sQuery(id+"F0.wireOp",EDGE,"E71"),sQuery(id+"F0.wireOp",EDGE,"E72"),sQuery(id+"F0.wireOp",EDGE,"E73"),sQuery(id+"F0.wireOp",EDGE,"E74"),sQuery(id+"F0.wireOp",EDGE,"E75"),sQuery(id+"F0.wireOp",EDGE,"E76"),sQuery(id+"F0.wireOp",EDGE,"E77"),sQuery(id+"F0.wireOp",EDGE,"E78"),sQuery(id+"F0.wireOp",EDGE,"E79"),sQuery(id+"F0.wireOp",EDGE,"E80"),sQuery(id+"F0.wireOp",EDGE,"E81"),sQuery(id+"F0.wireOp",EDGE,"E82"),sQuery(id+"F0.wireOp",EDGE,"E83"),sQuery(id+"F0.wireOp",EDGE,"E84"),sQuery(id+"F0.wireOp",EDGE,"E85"),sQuery(id+"F0.wireOp",EDGE,"E86"),sQuery(id+"F0.wireOp",EDGE,"E87"),sQuery(id+"F0.wireOp",EDGE,"E88"),sQuery(id+"F0.wireOp",EDGE,"PkSCfb9l-bHuo-pSPV-febg-RSfLSyBgUNz0"),sQuery(id+"F0.wireOp",EDGE,"E89"),subQ2,sQuery(id+"F0.wireOp",EDGE,"E90.left"),sQuery(id+"F0.wireOp",EDGE,"E90.right"),subQ1,subQ0,sQuery(id+"F0.wireOp",EDGE,"E93"),sQuery(id+"F0.wireOp",EDGE,"E95"),sQuery(id+"F0.wireOp",EDGE,"E96"),sQuery(id+"F0.wireOp",EDGE,"E97"),sQuery(id+"F0.wireOp",EDGE,"E98"),sQuery(id+"F0.wireOp",EDGE,"E99"),sQuery(id+"F0.wireOp",EDGE,"E100"),sQuery(id+"F0.wireOp",EDGE,"E101"),sQuery(id+"F0.wireOp",EDGE,"E103"),sQuery(id+"F0.wireOp",EDGE,"E104"),sQuery(id+"F0.wireOp",EDGE,"E105"),sQuery(id+"F0.wireOp",EDGE,"E106"),sQuery(id+"F0.wireOp",EDGE,"E107"),sQuery(id+"F0.wireOp",EDGE,"E108"),sQuery(id+"F0.wireOp",EDGE,"E109"),sQuery(id+"F0.wireOp",EDGE,"E110"),sQuery(id+"F0.wireOp",EDGE,"E111"),sQuery(id+"F0.wireOp",EDGE,"E112"),sQuery(id+"F0.wireOp",EDGE,"E113"),sQuery(id+"F0.wireOp",EDGE,"E114"),sQuery(id+"F0.wireOp",EDGE,"E115")])],"isStart":true})});}
            extrude(context, id + "F8", {"entities" : qUnion([Q0]), "operationType" : NewBodyOperationType.ADD, "depth" : 4 * mm});
        }
    });
